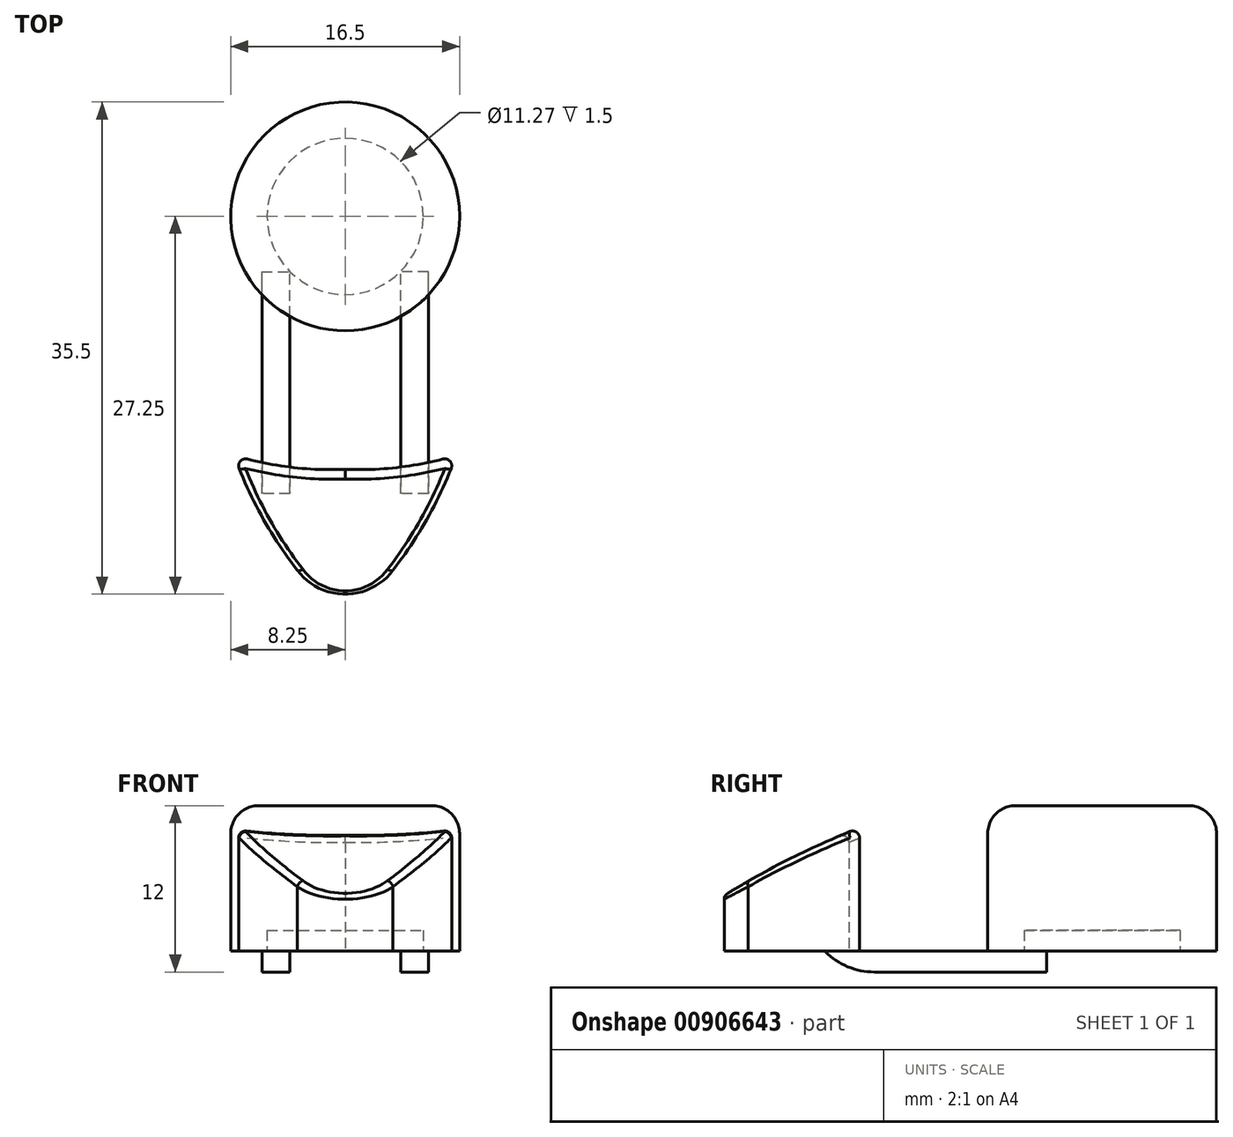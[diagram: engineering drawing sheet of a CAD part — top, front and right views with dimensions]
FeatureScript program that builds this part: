
annotation { "Feature Type Name" : "Feature", "Feature Type Description" : "" }
export const myFeature = defineFeature(function(context is Context, id is Id, definition is map)
    precondition{}
    {
        {
            var Q0;
            Q0=qCreatedBy(makeId("Top.planeOp"),FACE);
            var sketch = newSketch(context, id + "F0", { "sketchPlane" : qUnion([Q0])});
            skCircle(sketch, "E0", {"center": v(0, 0) * mm, "radius": 8.25 * mm});
            skLineSegment(sketch, "E1", {"start": v(-94.4, -27.25) * mm, "end": v(107.42, -27.25) * mm, "construction": true});
            skLineSegment(sketch, "E2", {"start": v(-8, 54.93) * mm, "end": v(-8, -65.66) * mm, "construction": true});
            skLineSegment(sketch, "E3", {"start": v(0, 57.48) * mm, "end": v(0, -55.95) * mm, "construction": true});
            skLineSegment(sketch, "E4", {"start": v(8, 54.93) * mm, "end": v(8, -62.08) * mm, "construction": true});
            skArc(sketch, "E5", {"start": v(0, -18.25) * mm, "mid": v(4.04, -18.08) * mm, "end": v(8, -17.25) * mm});
            skArc(sketch, "E6", {"start": v(0, -27.25) * mm, "mid": v(1.93, -26.8) * mm, "end": v(3.45, -25.52) * mm});
            skArc(sketch, "E7", {"start": v(3.45, -25.52) * mm, "mid": v(6.05, -21.56) * mm, "end": v(8, -17.25) * mm});
            skLineSegment(sketch, "E8.trimOffspring", {"start": v(0, -18.25) * mm, "end": v(103.6, -18.25) * mm, "construction": true});
            skArc(sketch, "E9.MirrorCS", {"start": v(0, -18.25) * mm, "mid": v(-4.04, -18.08) * mm, "end": v(-8, -17.25) * mm});
            skArc(sketch, "E10.MirrorCS", {"start": v(-3.45, -25.52) * mm, "mid": v(-6.05, -21.56) * mm, "end": v(-8, -17.25) * mm});
            skArc(sketch, "E11.MirrorCS", {"start": v(0, -27.25) * mm, "mid": v(-1.93, -26.8) * mm, "end": v(-3.45, -25.52) * mm});
            skSolve(sketch);
        }
        {
            var Q0;
            Q0 = qSketchRegion(id + "F0", true);
            extrude(context, id + "F1", {"entities" : qUnion([Q0]), "depth" : 9 * mm, "offsetDistance" : 25 * mm});
        }
        {
            var Q0;
            Q0=qCreatedBy(makeId("Right.planeOp"),FACE);
            var sketch = newSketch(context, id + "F2", { "sketchPlane" : qUnion([Q0])});
            skLineSegment(sketch, "E12.0.0", {"start": v(-25.52, 0) * mm, "end": v(-17.25, 0) * mm});
            skLineSegment(sketch, "E12.0.1", {"start": v(-17.25, 0) * mm, "end": v(-17.25, 9) * mm});
            skLineSegment(sketch, "E12.0.2", {"start": v(-17.25, 9) * mm, "end": v(-25.52, 9) * mm});
            skLineSegment(sketch, "E12.0.3", {"start": v(-25.52, 9) * mm, "end": v(-25.52, 0) * mm});
            skLineSegment(sketch, "E13", {"start": v(-27.25, -0.98) * mm, "end": v(-27.25, 9) * mm});
            skPoint(sketch, "E14", {"position": v(-27.25, 4.02) * mm});
            skArc(sketch, "E15", {"start": v(-17.25, 9) * mm, "mid": v(-22.37, 6.74) * mm, "end": v(-27.25, 4.02) * mm});
            skLineSegment(sketch, "E16", {"start": v(-27.25, 4.02) * mm, "end": v(-27.25, 9) * mm});
            skLineSegment(sketch, "E17", {"start": v(-27.25, 9) * mm, "end": v(-25.52, 9) * mm});
            skSolve(sketch);
        }
        {
            var Q0;
            {var subQ0=sQuery(id+"F2.wireOp",EDGE,"E12.0.2");Q0=makeQuery(id+"F2.imprint","IMPRINT",FACE,{"disambiguationData":[TD([[makeQuery(id+"F2.imprint","IMPRINT",EDGE,{"derivedFrom":subQ0}),1.0]])]});}
            var Q1;
            {var subQ0=sQuery(id+"F2.wireOp",EDGE,"E17");Q1=makeQuery(id+"F2.imprint","IMPRINT",FACE,{"disambiguationData":[TD([[makeQuery(id+"F2.imprint","IMPRINT",EDGE,{"derivedFrom":subQ0}),-1.0]])]});}
            extrude(context, id + "F3", {"entities" : qUnion([Q0, Q1]), "operationType" : NewBodyOperationType.REMOVE, "endBound" : BoundingType.SYMMETRIC, "depth" : 25 * mm, "offsetDistance" : 25 * mm});
        }
        {
            var Q0;
            Q0=makeQuery(id+"F1.opExtrude","SWEPT_EDGE",EDGE,{"disambiguationData":[OSD([sQuery(id+"F0.wireOp",EDGE,"E5"),sQuery(id+"F0.wireOp",EDGE,"E7")])]});
            var Q1;
            Q1=makeQuery(id+"F1.opExtrude","SWEPT_EDGE",EDGE,{"disambiguationData":[OSD([sQuery(id+"F0.wireOp",EDGE,"E9.MirrorCS"),sQuery(id+"F0.wireOp",EDGE,"E10.MirrorCS")])]});
            var Q2;
            Q2=makeQuery(id+"F3.boolean.opBoolean","COPY",FACE,{"derivedFrom":makeQuery(id+"F3.opExtrude","SWEPT_FACE",FACE,{"disambiguationData":[OSD([sQuery(id+"F2.wireOp",EDGE,"E15")])]})});
            fillet(context, id + "F4", {"entities" : qUnion([Q0, Q1, Q2]), "radius" : .5 * mm, "tangentPropagation" : true, "allowEdgeOverflow" : false});
        }
        {
            var Q0;
            Q0=qCreatedBy(makeId("Front.planeOp"),FACE);
            var sketch = newSketch(context, id + "F5", { "sketchPlane" : qUnion([Q0])});
            skLineSegment(sketch, "E18.0.0", {"start": v(8.25, 0) * mm, "end": v(-8.25, 0) * mm});
            skLineSegment(sketch, "E19", {"start": v(0, -8.72) * mm, "end": v(0, 11.69) * mm, "construction": true});
            skLineSegment(sketch, "E20", {"start": v(-6, -1.5) * mm, "end": v(0, -1.5) * mm});
            skLineSegment(sketch, "E21", {"start": v(0, -1.5) * mm, "end": v(0, 0) * mm});
            skLineSegment(sketch, "E22.MirrorCS", {"start": v(6, -1.5) * mm, "end": v(0, -1.5) * mm});
            skLineSegment(sketch, "E23.MirrorCS", {"start": v(-8.25, 0) * mm, "end": v(8.25, 0) * mm});
            skLineSegment(sketch, "E24", {"start": v(-6, -1.5) * mm, "end": v(-6, 0) * mm});
            skLineSegment(sketch, "E25", {"start": v(6, -1.5) * mm, "end": v(6, 0) * mm});
            skSolve(sketch);
        }
        {
            var Q0;
            Q0 = qSketchRegion(id + "F5", true);
            extrude(context, id + "F6", {"entities" : qUnion([Q0]), "operationType" : NewBodyOperationType.ADD, "depth" : 20 * mm, "offsetDistance" : 25 * mm});
        }
        {
            var Q0;
            Q0=makeQuery(id+"F6.opExtrude","CAP_FACE",FACE,{"disambiguationData":[OSD([sQuery(id+"F5.wireOp",EDGE,"E20"),sQuery(id+"F5.wireOp",EDGE,"E22.MirrorCS"),sQuery(id+"F5.wireOp",EDGE,"E23.MirrorCS"),sQuery(id+"F5.wireOp",EDGE,"E24"),sQuery(id+"F5.wireOp",EDGE,"E25")])],"isStart":true});
            var sketch = newSketch(context, id + "F7", { "sketchPlane" : qUnion([Q0])});
            skPoint(sketch, "E26", {"position": v(4, -1.5) * mm});
            skPoint(sketch, "E27.MirrorP", {"position": v(-4, -1.5) * mm});
            skLineSegment(sketch, "E28.bottom", {"start": v(4, -1.5) * mm, "end": v(-4, -1.5) * mm});
            skLineSegment(sketch, "E28.top", {"start": v(4, 0) * mm, "end": v(-4, 0) * mm});
            skLineSegment(sketch, "E28.left", {"start": v(4, -1.5) * mm, "end": v(4, 0) * mm});
            skLineSegment(sketch, "E28.right", {"start": v(-4, -1.5) * mm, "end": v(-4, 0) * mm});
            skSolve(sketch);
        }
        {
            var Q0;
            Q0 = qSketchRegion(id + "F7", true);
            extrude(context, id + "F8", {"entities" : qUnion([Q0]), "operationType" : NewBodyOperationType.REMOVE, "oppositeDirection" : true, "depth" : 25 * mm, "offsetDistance" : 25 * mm});
        }
        {
            var Q0;
            {var subQ0=sQuery(id+"F5.wireOp",EDGE,"E22.MirrorCS");var subQ1=sQuery(id+"F5.wireOp",EDGE,"E20");var subQ2=sQuery(id+"F5.wireOp",EDGE,"E24");Q0=makeQuery(id+"F8.boolean.opBoolean","SPLIT",FACE,{"disambiguationData":[TD([makeQuery(id+"F6.opExtrude","SWEPT_FACE",FACE,{"disambiguationData":[OSD([subQ2])]})])],"derivedFrom":makeQuery(id+"F6.opExtrude","CAP_FACE",FACE,{"disambiguationData":[OSD([subQ1,subQ0,sQuery(id+"F5.wireOp",EDGE,"E23.MirrorCS"),subQ2,sQuery(id+"F5.wireOp",EDGE,"E25")])],"isStart":true})});}
            var Q1;
            {var subQ0=sQuery(id+"F5.wireOp",EDGE,"E25");var subQ1=sQuery(id+"F5.wireOp",EDGE,"E22.MirrorCS");var subQ2=sQuery(id+"F5.wireOp",EDGE,"E20");Q1=makeQuery(id+"F8.boolean.opBoolean","SPLIT",FACE,{"disambiguationData":[TD([makeQuery(id+"F6.opExtrude","SWEPT_FACE",FACE,{"disambiguationData":[OSD([subQ0])]})])],"derivedFrom":makeQuery(id+"F6.opExtrude","CAP_FACE",FACE,{"disambiguationData":[OSD([subQ2,subQ1,sQuery(id+"F5.wireOp",EDGE,"E23.MirrorCS"),sQuery(id+"F5.wireOp",EDGE,"E24"),subQ0])],"isStart":true})});}
            extrude(context, id + "F9", {"entities" : qUnion([Q0, Q1]), "operationType" : NewBodyOperationType.REMOVE, "oppositeDirection" : true, "depth" : 4 * mm, "offsetDistance" : 25 * mm});
        }
        {
            var Q0;
            Q0=makeQuery(id+"F1.opExtrude","CAP_FACE",FACE,{"disambiguationData":[OSD([sQuery(id+"F0.wireOp",EDGE,"E0")])],"isStart":false});
            extrude(context, id + "F10", {"entities" : qUnion([Q0]), "operationType" : NewBodyOperationType.ADD, "depth" : 1.5 * mm, "offsetDistance" : 25 * mm});
        }
        {
            var Q0;
            Q0=makeQuery(id+"F10.opExtrude","CAP_FACE",FACE,{"disambiguationData":[OSD([sQuery(id+"F0.wireOp",EDGE,"E0")])],"isStart":false});
            fillet(context, id + "F11", {"entities" : qUnion([Q0]), "radius" : 2 * mm, "tangentPropagation" : true, "allowEdgeOverflow" : false});
        }
        {
            var Q0;
            {var subQ0=sQuery(id+"F5.wireOp",EDGE,"E22.MirrorCS");var subQ1=sQuery(id+"F5.wireOp",EDGE,"E20");var subQ2=sQuery(id+"F5.wireOp",EDGE,"E25");Q0=makeQuery(id+"F9.boolean.opBoolean","COPY",EDGE,{"derivedFrom":makeQuery(id+"F9.opExtrude","CAP_EDGE",EDGE,{"disambiguationData":[OSD([subQ1,subQ0]),TDD([makeQuery(id+"F8.boolean.opBoolean","SPLIT",EDGE,{"disambiguationData":[TD([makeQuery(id+"F6.opExtrude","SWEPT_FACE",FACE,{"disambiguationData":[OSD([subQ2])]})])],"derivedFrom":makeQuery(id+"F6.opExtrude","CAP_EDGE",EDGE,{"disambiguationData":[OSD([subQ1,subQ0])],"isStart":true})})])],"isStart":false})});}
            var Q1;
            {var subQ0=sQuery(id+"F5.wireOp",EDGE,"E22.MirrorCS");var subQ1=sQuery(id+"F5.wireOp",EDGE,"E20");var subQ2=sQuery(id+"F5.wireOp",EDGE,"E24");Q1=makeQuery(id+"F9.boolean.opBoolean","COPY",EDGE,{"derivedFrom":makeQuery(id+"F9.opExtrude","CAP_EDGE",EDGE,{"disambiguationData":[OSD([subQ1,subQ0]),TDD([makeQuery(id+"F8.boolean.opBoolean","SPLIT",EDGE,{"disambiguationData":[TD([makeQuery(id+"F6.opExtrude","SWEPT_FACE",FACE,{"disambiguationData":[OSD([subQ2])]})])],"derivedFrom":makeQuery(id+"F6.opExtrude","CAP_EDGE",EDGE,{"disambiguationData":[OSD([subQ1,subQ0])],"isStart":true})})])],"isStart":false})});}
            var Q2;
            {var subQ0=sQuery(id+"F5.wireOp",EDGE,"E22.MirrorCS");var subQ1=sQuery(id+"F5.wireOp",EDGE,"E20");var subQ2=sQuery(id+"F5.wireOp",EDGE,"E24");Q2=makeQuery(id+"F8.boolean.opBoolean","SPLIT",EDGE,{"disambiguationData":[TD([makeQuery(id+"F6.opExtrude","SWEPT_FACE",FACE,{"disambiguationData":[OSD([subQ2])]})])],"derivedFrom":makeQuery(id+"F6.opExtrude","CAP_EDGE",EDGE,{"disambiguationData":[OSD([subQ1,subQ0])],"isStart":false})});}
            var Q3;
            {var subQ0=sQuery(id+"F5.wireOp",EDGE,"E22.MirrorCS");var subQ1=sQuery(id+"F5.wireOp",EDGE,"E20");var subQ2=sQuery(id+"F5.wireOp",EDGE,"E25");Q3=makeQuery(id+"F8.boolean.opBoolean","SPLIT",EDGE,{"disambiguationData":[TD([makeQuery(id+"F6.opExtrude","SWEPT_FACE",FACE,{"disambiguationData":[OSD([subQ2])]})])],"derivedFrom":makeQuery(id+"F6.opExtrude","CAP_EDGE",EDGE,{"disambiguationData":[OSD([subQ1,subQ0])],"isStart":false})});}
            chamfer(context, id + "F12", {"entities" : qUnion([Q0, Q1, Q2, Q3]), "width" : 1.5 * mm, "tangentPropagation" : true});
        }
        {
            var Q0;
            {var subQ1=sQuery(id+"F5.wireOp",EDGE,"E24");var subQ3=sQuery(id+"F5.wireOp",EDGE,"E22.MirrorCS");var subQ4=sQuery(id+"F5.wireOp",EDGE,"E20");var subQ6=makeQuery(id+"F6.opExtrude","SWEPT_FACE",FACE,{"disambiguationData":[OSD([subQ1])]});var subQ8=makeQuery(id+"F6.opExtrude","SWEPT_FACE",FACE,{"disambiguationData":[OSD([subQ4,subQ3])]});Q0=makeQuery(id+"F12.opChamfer","BLEND_EDGE",EDGE,{"blendedFrom":[makeQuery(id+"F9.boolean.opBoolean","COPY",EDGE,{"derivedFrom":makeQuery(id+"F9.opExtrude","CAP_EDGE",EDGE,{"disambiguationData":[OSD([subQ4,subQ3]),TDD([makeQuery(id+"F8.boolean.opBoolean","SPLIT",EDGE,{"disambiguationData":[TD([subQ6])],"derivedFrom":makeQuery(id+"F6.opExtrude","CAP_EDGE",EDGE,{"disambiguationData":[OSD([subQ4,subQ3])],"isStart":true})})])],"isStart":false})}),makeQuery(id+"F8.boolean.opBoolean","SPLIT",FACE,{"disambiguationData":[TD([subQ6])],"derivedFrom":subQ8})],"blendedInto":[makeQuery(id+"F8.boolean.opBoolean","SPLIT",FACE,{"disambiguationData":[TD([subQ6])],"derivedFrom":subQ8})]});}
            var Q1;
            {var subQ0=sQuery(id+"F5.wireOp",EDGE,"E25");var subQ3=sQuery(id+"F5.wireOp",EDGE,"E22.MirrorCS");var subQ4=sQuery(id+"F5.wireOp",EDGE,"E20");var subQ6=makeQuery(id+"F6.opExtrude","SWEPT_FACE",FACE,{"disambiguationData":[OSD([subQ0])]});var subQ8=makeQuery(id+"F6.opExtrude","SWEPT_FACE",FACE,{"disambiguationData":[OSD([subQ4,subQ3])]});Q1=makeQuery(id+"F12.opChamfer","BLEND_EDGE",EDGE,{"blendedFrom":[makeQuery(id+"F9.boolean.opBoolean","COPY",EDGE,{"derivedFrom":makeQuery(id+"F9.opExtrude","CAP_EDGE",EDGE,{"disambiguationData":[OSD([subQ4,subQ3]),TDD([makeQuery(id+"F8.boolean.opBoolean","SPLIT",EDGE,{"disambiguationData":[TD([subQ6])],"derivedFrom":makeQuery(id+"F6.opExtrude","CAP_EDGE",EDGE,{"disambiguationData":[OSD([subQ4,subQ3])],"isStart":true})})])],"isStart":false})}),makeQuery(id+"F8.boolean.opBoolean","SPLIT",FACE,{"disambiguationData":[TD([subQ6])],"derivedFrom":subQ8})],"blendedInto":[makeQuery(id+"F8.boolean.opBoolean","SPLIT",FACE,{"disambiguationData":[TD([subQ6])],"derivedFrom":subQ8})]});}
            var Q2;
            {var subQ1=sQuery(id+"F5.wireOp",EDGE,"E24");var subQ3=sQuery(id+"F5.wireOp",EDGE,"E22.MirrorCS");var subQ4=sQuery(id+"F5.wireOp",EDGE,"E20");var subQ6=makeQuery(id+"F6.opExtrude","SWEPT_FACE",FACE,{"disambiguationData":[OSD([subQ1])]});var subQ8=makeQuery(id+"F6.opExtrude","SWEPT_FACE",FACE,{"disambiguationData":[OSD([subQ4,subQ3])]});Q2=makeQuery(id+"F12.opChamfer","BLEND_EDGE",EDGE,{"blendedFrom":[makeQuery(id+"F8.boolean.opBoolean","SPLIT",EDGE,{"disambiguationData":[TD([subQ6])],"derivedFrom":makeQuery(id+"F6.opExtrude","CAP_EDGE",EDGE,{"disambiguationData":[OSD([subQ4,subQ3])],"isStart":false})}),makeQuery(id+"F8.boolean.opBoolean","SPLIT",FACE,{"disambiguationData":[TD([subQ6])],"derivedFrom":subQ8})],"blendedInto":[makeQuery(id+"F8.boolean.opBoolean","SPLIT",FACE,{"disambiguationData":[TD([subQ6])],"derivedFrom":subQ8})]});}
            var Q3;
            {var subQ0=sQuery(id+"F5.wireOp",EDGE,"E25");var subQ3=sQuery(id+"F5.wireOp",EDGE,"E22.MirrorCS");var subQ4=sQuery(id+"F5.wireOp",EDGE,"E20");var subQ6=makeQuery(id+"F6.opExtrude","SWEPT_FACE",FACE,{"disambiguationData":[OSD([subQ0])]});var subQ8=makeQuery(id+"F6.opExtrude","SWEPT_FACE",FACE,{"disambiguationData":[OSD([subQ4,subQ3])]});Q3=makeQuery(id+"F12.opChamfer","BLEND_EDGE",EDGE,{"blendedFrom":[makeQuery(id+"F8.boolean.opBoolean","SPLIT",EDGE,{"disambiguationData":[TD([subQ6])],"derivedFrom":makeQuery(id+"F6.opExtrude","CAP_EDGE",EDGE,{"disambiguationData":[OSD([subQ4,subQ3])],"isStart":false})}),makeQuery(id+"F8.boolean.opBoolean","SPLIT",FACE,{"disambiguationData":[TD([subQ6])],"derivedFrom":subQ8})],"blendedInto":[makeQuery(id+"F8.boolean.opBoolean","SPLIT",FACE,{"disambiguationData":[TD([subQ6])],"derivedFrom":subQ8})]});}
            fillet(context, id + "F13", {"entities" : qUnion([Q0, Q1, Q2, Q3]), "radius" : 5 * mm, "tangentPropagation" : true, "allowEdgeOverflow" : false});
        }
        {
            var Q0;
            {var subQ0=makeQuery(id+"F8.opExtrude","SWEPT_FACE",FACE,{"disambiguationData":[OSD([sQuery(id+"F7.wireOp",EDGE,"E28.top")])]});var subQ1=sQuery(id+"F5.wireOp",EDGE,"E25");var subQ2=sQuery(id+"F5.wireOp",EDGE,"E24");var subQ3=sQuery(id+"F5.wireOp",EDGE,"E23.MirrorCS");var subQ5=makeQuery(id+"F1.opExtrude","CAP_FACE",FACE,{"disambiguationData":[OSD([sQuery(id+"F0.wireOp",EDGE,"E0")])],"isStart":true});var subQ6=makeQuery(id+"F6.opExtrude","CAP_EDGE",EDGE,{"disambiguationData":[OSD([subQ3])],"isStart":true});Q0=makeQuery(id+"F9.boolean.opBoolean","MERGE",FACE,{"derivedFrom":[makeQuery(id+"F8.boolean.opBoolean","MERGE",FACE,{"derivedFrom":[subQ5],"fromTools":[subQ0]})],"fromTools":[makeQuery(id+"F9.opExtrude","SWEPT_FACE",FACE,{"disambiguationData":[OSD([subQ3]),TDD([makeQuery(id+"F8.boolean.opBoolean","SPLIT",EDGE,{"disambiguationData":[TD([makeQuery(id+"F6.opExtrude","SWEPT_FACE",FACE,{"disambiguationData":[OSD([subQ2])]})])],"derivedFrom":subQ6})])]}),makeQuery(id+"F9.opExtrude","SWEPT_FACE",FACE,{"disambiguationData":[OSD([subQ3]),TDD([makeQuery(id+"F8.boolean.opBoolean","SPLIT",EDGE,{"disambiguationData":[TD([makeQuery(id+"F6.opExtrude","SWEPT_FACE",FACE,{"disambiguationData":[OSD([subQ1])]})])],"derivedFrom":subQ6})])]})]});}
            var sketch = newSketch(context, id + "F14", { "sketchPlane" : qUnion([Q0])});
            skCircle(sketch, "E29", {"center": v(0, 0) * mm, "radius": 5.63 * mm});
            skSolve(sketch);
        }
        {
            var Q0;
            Q0 = qSketchRegion(id + "F14", true);
            extrude(context, id + "F15", {"entities" : qUnion([Q0]), "operationType" : NewBodyOperationType.REMOVE, "oppositeDirection" : true, "depth" : 1.5 * mm, "offsetDistance" : 25 * mm});
        }
    });
